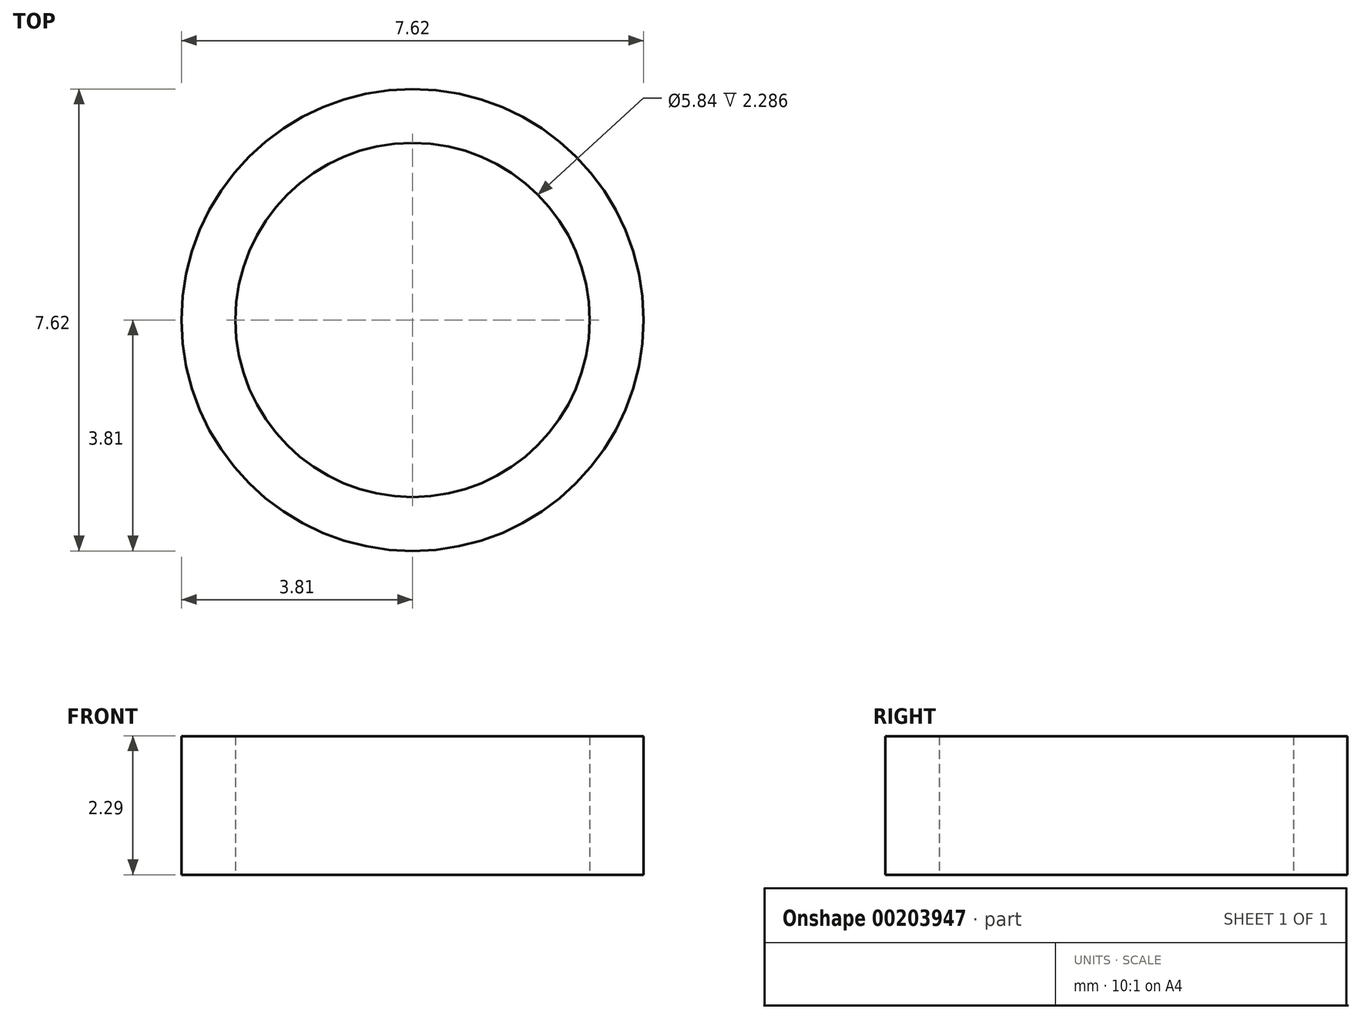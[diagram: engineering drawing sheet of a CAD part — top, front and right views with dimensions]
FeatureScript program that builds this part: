
annotation { "Feature Type Name" : "Feature", "Feature Type Description" : "" }
export const myFeature = defineFeature(function(context is Context, id is Id, definition is map)
    precondition{}
    {
        {
            var Q0;
            Q0=qCreatedBy(makeId("Top.planeOp"),FACE);
            var sketch = newSketch(context, id + "F0", { "sketchPlane" : qUnion([Q0])});
            skCircle(sketch, "E0", {"center": v(0, 0) * mm, "radius": 2.92 * mm});
            skCircle(sketch, "E1", {"center": v(0, 0) * mm, "radius": 3.81 * mm});
            skSolve(sketch);
        }
        {
            var Q0;
            Q0 = qSketchRegion(id + "F0", true);
            extrude(context, id + "F1", {"entities" : qUnion([Q0]), "depth" : 2.3 * mm});
        }
    });
